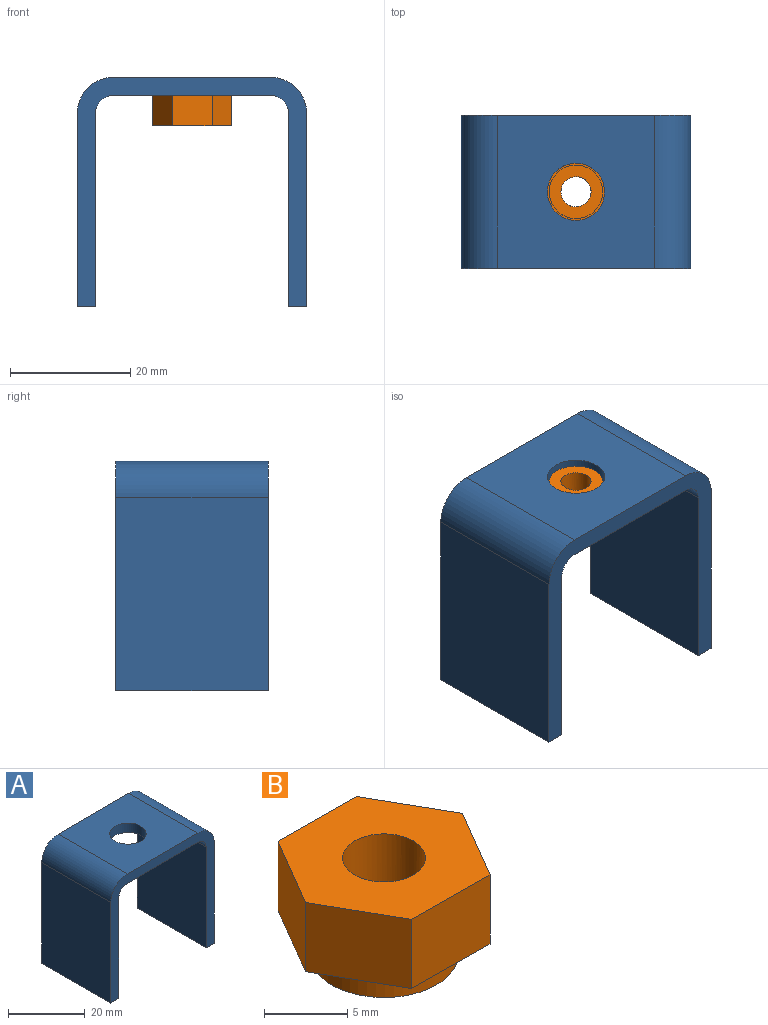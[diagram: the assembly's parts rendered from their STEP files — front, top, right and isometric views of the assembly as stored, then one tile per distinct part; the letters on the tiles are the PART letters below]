
ASSEMBLY  parts=2 mates=1
PART A: 15 faces, bbox 38.1x25.4x38.1 mm
  f0: cylinder r=3mm len=25.4mm, axis (0,1,0), area 119.7mm2, adj f1,f11,f12,f13
  f1: plane 26.1x25.4mm, normal (0,0,-1), area 592.1mm2, adj f0,f2,f12,f13,f14
  f2: cylinder r=3mm len=25.4mm, axis (0,1,0), area 119.7mm2, adj f1,f3,f12,f13
  f3: plane 32.1x25.4mm, normal (-1,0,0), area 815.3mm2, adj f2,f4,f12,f13
  f4: plane 25.4x3mm, normal (0,0,-1), area 76.2mm2, adj f3,f5,f12,f13
  f5: plane 32.1x25.4mm, normal (1,0,0), area 815.3mm2, adj f4,f6,f12,f13
  f6: cylinder r=6mm len=25.4mm, axis (0,1,0), area 239.4mm2, adj f5,f7,f12,f13
  f7: plane 26.1x25.4mm, normal (0,0,1), area 592.1mm2, adj f6,f8,f12,f13,f14
  f8: cylinder r=6mm len=25.4mm, axis (0,1,0), area 239.4mm2, adj f7,f9,f12,f13
  f9: plane 32.1x25.4mm, normal (-1,0,0), area 815.3mm2, adj f8,f10,f12,f13
  f10: plane 25.4x3mm, normal (0,0,-1), area 76.2mm2, adj f9,f11,f12,f13
  f11: plane 32.1x25.4mm, normal (1,0,0), area 815.3mm2, adj f0,f10,f12,f13
  f12: plane 38.1x38.1mm, normal (0,-1,0), area 313.3mm2, adj f0,f1,f2,f3,f4,f5,f6,f7
  f13: plane 38.1x38.1mm, normal (0,1,0), area 313.3mm2, adj f0,f1,f2,f3,f4,f5,f6,f7
  f14: cylinder r=4.75mm len=9.5mm, axis (0,0,1), area 89.5mm2, adj f1,f7
PART B: 11 faces, bbox 13.2x11.5x7.1 mm
  f0: plane 5.69x5.08mm, normal (-0.86,0.51,0), area 33.5mm2, adj f1,f5,f6,f7
  f1: plane 5.74x5.08mm, normal (-0.87,-0.49,0), area 33.5mm2, adj f0,f2,f6,f7
  f2: plane 6.6x5.08mm, normal (-0.01,-1,0), area 33.5mm2, adj f1,f3,f6,f7
  f3: plane 5.69x5.08mm, normal (0.86,-0.51,0), area 33.5mm2, adj f2,f4,f6,f7
  f4: plane 5.74x5.08mm, normal (0.87,0.49,0), area 33.5mm2, adj f3,f5,f6,f7
  f5: plane 6.6x5.08mm, normal (0.01,1,0), area 33.5mm2, adj f0,f4,f6,f7
  f6: plane 13.2x11.48mm, normal (0,0,1), area 93.5mm2, adj f0,f1,f2,f3,f4,f5,f10
  f7: plane 13.2x11.48mm, normal (0,0,-1), area 51.1mm2, adj f0,f1,f2,f3,f4,f5,f8
  f8: cylinder r=4.45mm len=8.89mm, axis (0,0,1), area 56.8mm2, adj f7,f9
  f9: plane 8.89x8.89mm, normal (0,0,-1), area 42.4mm2, adj f8,f10
  f10: cylinder r=2.5mm len=7.11mm, axis (0,0,-1), area 111.7mm2, adj f6,f9
PLACE A t=(-0.99,2.91,0)mm fixed
PLACE B rot(axis=(1,0,0),180deg) t=(-0.99,2.91,-3)mm
MATE fastened B.f8 <-> A.f14  axis (0,0,1) through (-0.99,2.91,-3)mm
